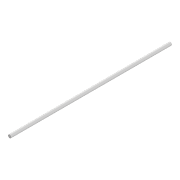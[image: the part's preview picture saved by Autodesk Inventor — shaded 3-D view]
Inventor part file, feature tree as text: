
AUTODESK INVENTOR PART (.ipt)
format: ipt  version: 2021 (Build 250183000, 183)  size: 70,656 bytes
history: native  units: mm
features: extrude x1, sketch x1
ambient origin geometry x8: Origin, YZ Plane, XZ Plane, XY Plane, X Axis, Y Axis, Z Axis, Center Point
bodies: 实体1 (feature_tree)
feature tree (2):
  extrude  "拉伸1"  Depth=510.0mm TaperAngle=0.0deg
  sketch  "草图1"  dims[d0=10.0mm d1=510.0mm d2=0.0mm]
